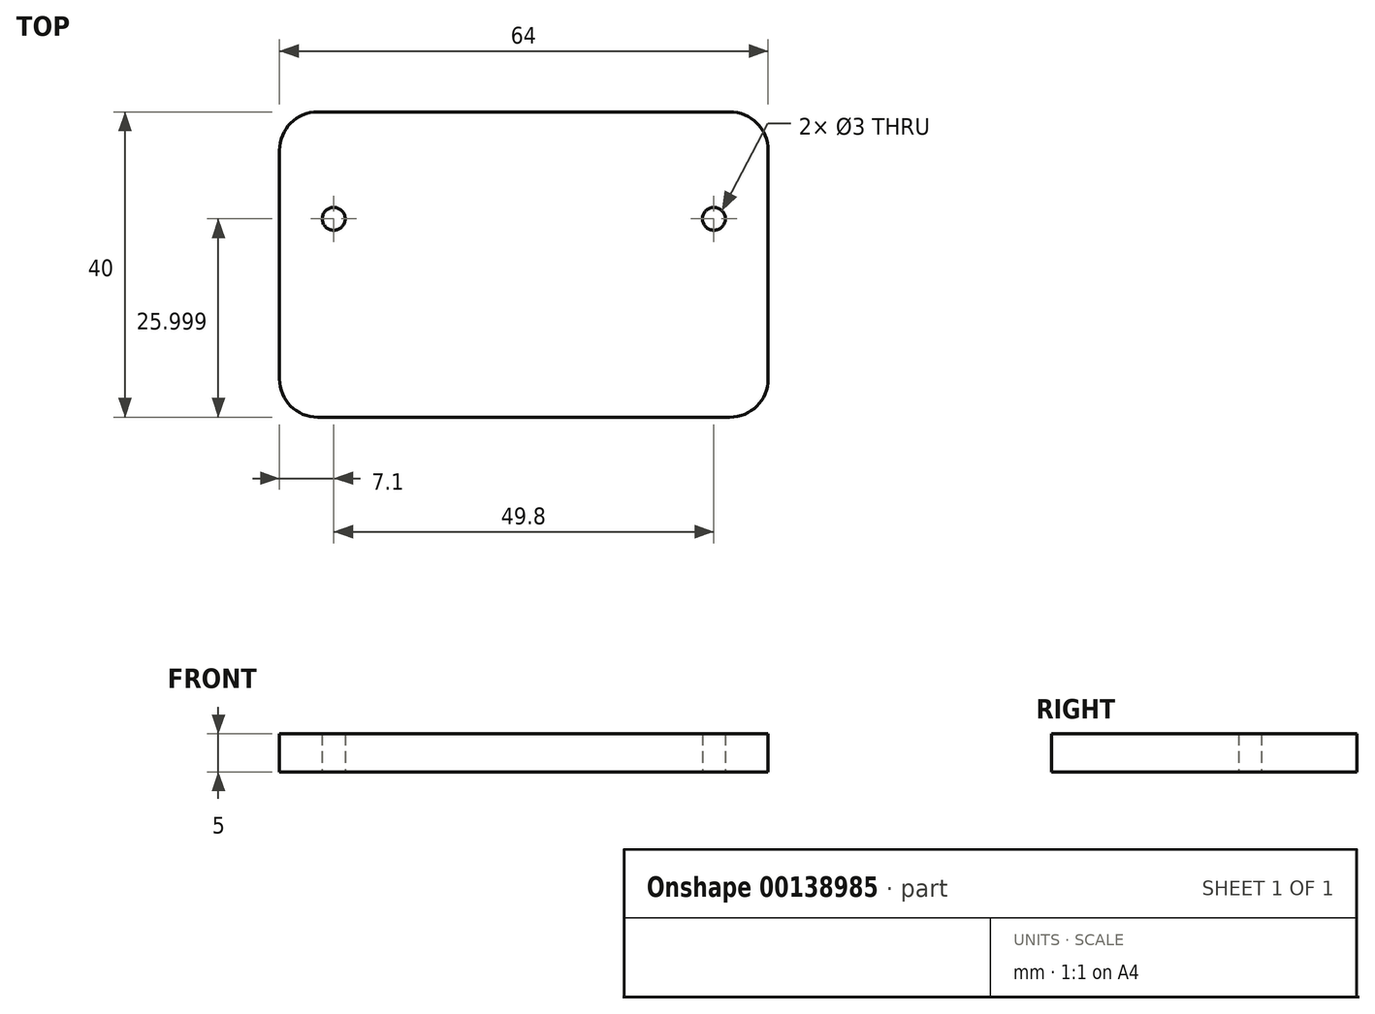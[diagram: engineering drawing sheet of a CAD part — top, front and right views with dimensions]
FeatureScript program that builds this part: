
annotation { "Feature Type Name" : "Feature", "Feature Type Description" : "" }
export const myFeature = defineFeature(function(context is Context, id is Id, definition is map)
    precondition{}
    {
        {
            var Q0;
            Q0=qCreatedBy(makeId("Top.planeOp"),FACE);
            var sketch = newSketch(context, id + "F0", { "sketchPlane" : qUnion([Q0])});
            skLineSegment(sketch, "E0.bottom", {"start": v(-32, -15.98) * mm, "end": v(32, -15.98) * mm});
            skLineSegment(sketch, "E0.top", {"start": v(-32, -55.98) * mm, "end": v(32, -55.98) * mm});
            skLineSegment(sketch, "E0.left", {"start": v(-32, -15.98) * mm, "end": v(-32, -55.98) * mm});
            skLineSegment(sketch, "E0.right", {"start": v(32, -15.98) * mm, "end": v(32, -55.98) * mm});
            skPoint(sketch, "E1", {"position": v(0, -15.98) * mm});
            skCircle(sketch, "E2", {"center": v(-24.9, -29.98) * mm, "radius": 1.5 * mm});
            skCircle(sketch, "E3", {"center": v(24.9, -29.98) * mm, "radius": 1.5 * mm});
            skLineSegment(sketch, "E4", {"start": v(-24.9, -29.98) * mm, "end": v(24.9, -29.98) * mm, "construction": true});
            skPoint(sketch, "E5", {"position": v(0, -29.98) * mm});
            skSolve(sketch);
        }
        {
            var Q0;
            {var subQ0=sQuery(id+"F0.wireOp",EDGE,"jERFmMc1-pHtx-xSjX-CREn-mMAGXFSP4TBY");Q0=makeQuery(id+"F0.imprint","IMPRINT",FACE,{"disambiguationData":[TD([[makeQuery(id+"F0.imprint","IMPRINT",EDGE,{"derivedFrom":subQ0}),1.0]])]});}
            var Q1;
            {var subQ1=sQuery(id+"F0.wireOp",EDGE,"67b553d4-da37-4b79-837f-7390a9b511f5.1");var subQ3=sQuery(id+"F0.wireOp",EDGE,"COOTdLvE-wemh-VFDn-cW9V-s5y5DAECa6rX");var subQ4=makeQuery(id+"F0.imprint","INTERSECT",VERTEX,{"disambiguationData":[OD(1.0)],"derivedFrom":[subQ1,subQ3]});Q1=makeQuery(id+"F0.imprint","IMPRINT",FACE,{"disambiguationData":[TD([[makeQuery(id+"F0.imprint","IMPRINT",EDGE,{"disambiguationData":[TD([[subQ4,1.0]])],"derivedFrom":subQ3}),-1.0]])]});}
            var Q2;
            {var subQ0=sQuery(id+"F0.wireOp",EDGE,"VufKUYgK-xRFZ-ZU3I-uEfZ-TcgWjPXBH8dB");Q2=makeQuery(id+"F0.imprint","IMPRINT",FACE,{"disambiguationData":[TD([[makeQuery(id+"F0.imprint","IMPRINT",EDGE,{"derivedFrom":subQ0}),1.0]])]});}
            var Q3;
            {var subQ13=sQuery(id+"F0.wireOp",EDGE,"8JRTccjr-kDRW-iMPo-pbyM-UjpLYdR7sCPQ.top");Q3=makeQuery(id+"F0.imprint","IMPRINT",FACE,{"disambiguationData":[TD([[makeQuery(id+"F0.imprint","IMPRINT",EDGE,{"derivedFrom":subQ13}),-1.0]])]});}
            var Q4;
            {var subQ5=sQuery(id+"F0.wireOp",EDGE,"8JRTccjr-kDRW-iMPo-pbyM-UjpLYdR7sCPQ.bottom");Q4=makeQuery(id+"F0.imprint","IMPRINT",FACE,{"disambiguationData":[TD([[makeQuery(id+"F0.imprint","IMPRINT",EDGE,{"derivedFrom":subQ5}),-1.0]])]});}
            var Q5;
            {var subQ0=sQuery(id+"F0.wireOp",EDGE,"8JRTccjr-kDRW-iMPo-pbyM-UjpLYdR7sCPQ.left");var subQ1=sQuery(id+"F0.wireOp",EDGE,"67b553d4-da37-4b79-837f-7390a9b511f5.0");var subQ2=makeQuery(id+"F0.imprint","INTERSECT",VERTEX,{"derivedFrom":[subQ1,subQ0]});Q5=makeQuery(id+"F0.imprint","IMPRINT",FACE,{"disambiguationData":[TD([[makeQuery(id+"F0.imprint","IMPRINT",EDGE,{"disambiguationData":[TD([[subQ2,-1.0]])],"derivedFrom":subQ1}),-1.0]])]});}
            var Q6;
            {var subQ5=sQuery(id+"F0.wireOp",EDGE,"8JRTccjr-kDRW-iMPo-pbyM-UjpLYdR7sCPQ.top");Q6=makeQuery(id+"F0.imprint","IMPRINT",FACE,{"disambiguationData":[TD([[makeQuery(id+"F0.imprint","IMPRINT",EDGE,{"derivedFrom":subQ5}),1.0]])]});}
            var Q7;
            {var subQ0=sQuery(id+"F0.wireOp",EDGE,"COOTdLvE-wemh-VFDn-cW9V-s5y5DAECa6rX");var subQ1=sQuery(id+"F0.wireOp",EDGE,"vwtUNxXE-5amK-ixxl-kl4G-om5iWZnCJFOI");var subQ2=makeQuery(id+"F0.imprint","INTERSECT",VERTEX,{"disambiguationData":[OD(0.0)],"derivedFrom":[subQ1,subQ0]});Q7=makeQuery(id+"F0.imprint","IMPRINT",FACE,{"disambiguationData":[TD([[makeQuery(id+"F0.imprint","IMPRINT",EDGE,{"disambiguationData":[TD([[subQ2,-1.0]])],"derivedFrom":subQ1}),1.0]])]});}
            var Q8;
            {var subQ0=sQuery(id+"F0.wireOp",EDGE,"COOTdLvE-wemh-VFDn-cW9V-s5y5DAECa6rX");var subQ1=sQuery(id+"F0.wireOp",EDGE,"67b553d4-da37-4b79-837f-7390a9b511f5.0");var subQ2=makeQuery(id+"F0.imprint","INTERSECT",VERTEX,{"disambiguationData":[OD(0.0)],"derivedFrom":[subQ1,subQ0]});Q8=makeQuery(id+"F0.imprint","IMPRINT",FACE,{"disambiguationData":[TD([[makeQuery(id+"F0.imprint","IMPRINT",EDGE,{"disambiguationData":[TD([[subQ2,-1.0]])],"derivedFrom":subQ1}),1.0]])]});}
            var Q9;
            {var subQ0=sQuery(id+"F0.wireOp",EDGE,"COOTdLvE-wemh-VFDn-cW9V-s5y5DAECa6rX");var subQ1=sQuery(id+"F0.wireOp",EDGE,"67b553d4-da37-4b79-837f-7390a9b511f5.1");var subQ2=makeQuery(id+"F0.imprint","INTERSECT",VERTEX,{"disambiguationData":[OD(0.0)],"derivedFrom":[subQ1,subQ0]});Q9=makeQuery(id+"F0.imprint","IMPRINT",FACE,{"disambiguationData":[TD([[makeQuery(id+"F0.imprint","IMPRINT",EDGE,{"disambiguationData":[TD([[subQ2,-1.0]])],"derivedFrom":subQ0}),-1.0]])]});}
            var Q10;
            {var subQ0=sQuery(id+"F0.wireOp",EDGE,"COOTdLvE-wemh-VFDn-cW9V-s5y5DAECa6rX");var subQ1=sQuery(id+"F0.wireOp",EDGE,"67b553d4-da37-4b79-837f-7390a9b511f5.2");var subQ2=makeQuery(id+"F0.imprint","INTERSECT",VERTEX,{"disambiguationData":[OD(1.0)],"derivedFrom":[subQ1,subQ0]});Q10=makeQuery(id+"F0.imprint","IMPRINT",FACE,{"disambiguationData":[TD([[makeQuery(id+"F0.imprint","IMPRINT",EDGE,{"disambiguationData":[TD([[subQ2,1.0]])],"derivedFrom":subQ0}),-1.0]])]});}
            var Q11;
            {var subQ0=sQuery(id+"F0.wireOp",EDGE,"E0.top");Q11=makeQuery(id+"F0.imprint","IMPRINT",FACE,{"disambiguationData":[TD([[makeQuery(id+"F0.imprint","IMPRINT",EDGE,{"derivedFrom":subQ0}),1.0]])]});}
            extrude(context, id + "F1", {"entities" : qUnion([Q0, Q1, Q2, Q3, Q4, Q5, Q6, Q7, Q8, Q9, Q10, Q11]), "depth" : 5 * mm});
        }
        {
            var Q0;
            Q0=makeQuery(id+"F1.opExtrude","SWEPT_EDGE",EDGE,{"disambiguationData":[OSD([sQuery(id+"F0.wireOp",EDGE,"67b553d4-da37-4b79-837f-7390a9b511f5.0"),sQuery(id+"F0.wireOp",EDGE,"E0.left")])]});
            var Q1;
            Q1=makeQuery(id+"F1.opExtrude","SWEPT_EDGE",EDGE,{"disambiguationData":[OSD([sQuery(id+"F0.wireOp",EDGE,"67b553d4-da37-4b79-837f-7390a9b511f5.0"),sQuery(id+"F0.wireOp",EDGE,"67b553d4-da37-4b79-837f-7390a9b511f5.1"),sQuery(id+"F0.wireOp",EDGE,"jERFmMc1-pHtx-xSjX-CREn-mMAGXFSP4TBY")])]});
            var Q2;
            Q2=makeQuery(id+"F1.opExtrude","SWEPT_EDGE",EDGE,{"disambiguationData":[OSD([sQuery(id+"F0.wireOp",EDGE,"67b553d4-da37-4b79-837f-7390a9b511f5.0"),sQuery(id+"F0.wireOp",EDGE,"E0.right")])]});
            var Q3;
            Q3=makeQuery(id+"F1.opExtrude","SWEPT_EDGE",EDGE,{"disambiguationData":[OSD([sQuery(id+"F0.wireOp",EDGE,"67b553d4-da37-4b79-837f-7390a9b511f5.0"),sQuery(id+"F0.wireOp",EDGE,"67b553d4-da37-4b79-837f-7390a9b511f5.2"),sQuery(id+"F0.wireOp",EDGE,"VufKUYgK-xRFZ-ZU3I-uEfZ-TcgWjPXBH8dB")])]});
            var Q4;
            Q4=makeQuery(id+"F1.opExtrude","SWEPT_EDGE",EDGE,{"disambiguationData":[OSD([sQuery(id+"F0.wireOp",EDGE,"E0.top"),sQuery(id+"F0.wireOp",EDGE,"E0.left")])]});
            var Q5;
            Q5=makeQuery(id+"F1.opExtrude","SWEPT_EDGE",EDGE,{"disambiguationData":[OSD([sQuery(id+"F0.wireOp",EDGE,"E0.top"),sQuery(id+"F0.wireOp",EDGE,"E0.right")])]});
            var Q6;
            {var subQ0=sQuery(id+"F0.wireOp",EDGE,"E0.bottom");var subQ1=sQuery(id+"F0.wireOp",EDGE,"COOTdLvE-wemh-VFDn-cW9V-s5y5DAECa6rX");Q6=makeQuery(id+"F1.opExtrude","SWEPT_EDGE",EDGE,{"disambiguationData":[OSD([subQ1,subQ0]),TDD([makeQuery(id+"F0.imprint","INTERSECT",VERTEX,{"disambiguationData":[OD(0.0)],"derivedFrom":[subQ1,subQ0]})])]});}
            var Q7;
            {var subQ0=sQuery(id+"F0.wireOp",EDGE,"E0.bottom");var subQ1=sQuery(id+"F0.wireOp",EDGE,"COOTdLvE-wemh-VFDn-cW9V-s5y5DAECa6rX");Q7=makeQuery(id+"F1.opExtrude","SWEPT_EDGE",EDGE,{"disambiguationData":[OSD([subQ1,subQ0]),TDD([makeQuery(id+"F0.imprint","INTERSECT",VERTEX,{"disambiguationData":[OD(1.0)],"derivedFrom":[subQ1,subQ0]})])]});}
            fillet(context, id + "F2", {"entities" : qUnion([Q0, Q1, Q2, Q3, Q4, Q5, Q6, Q7]), "radius" : 5 * mm, "tangentPropagation" : true, "allowEdgeOverflow" : false});
        }
    });
